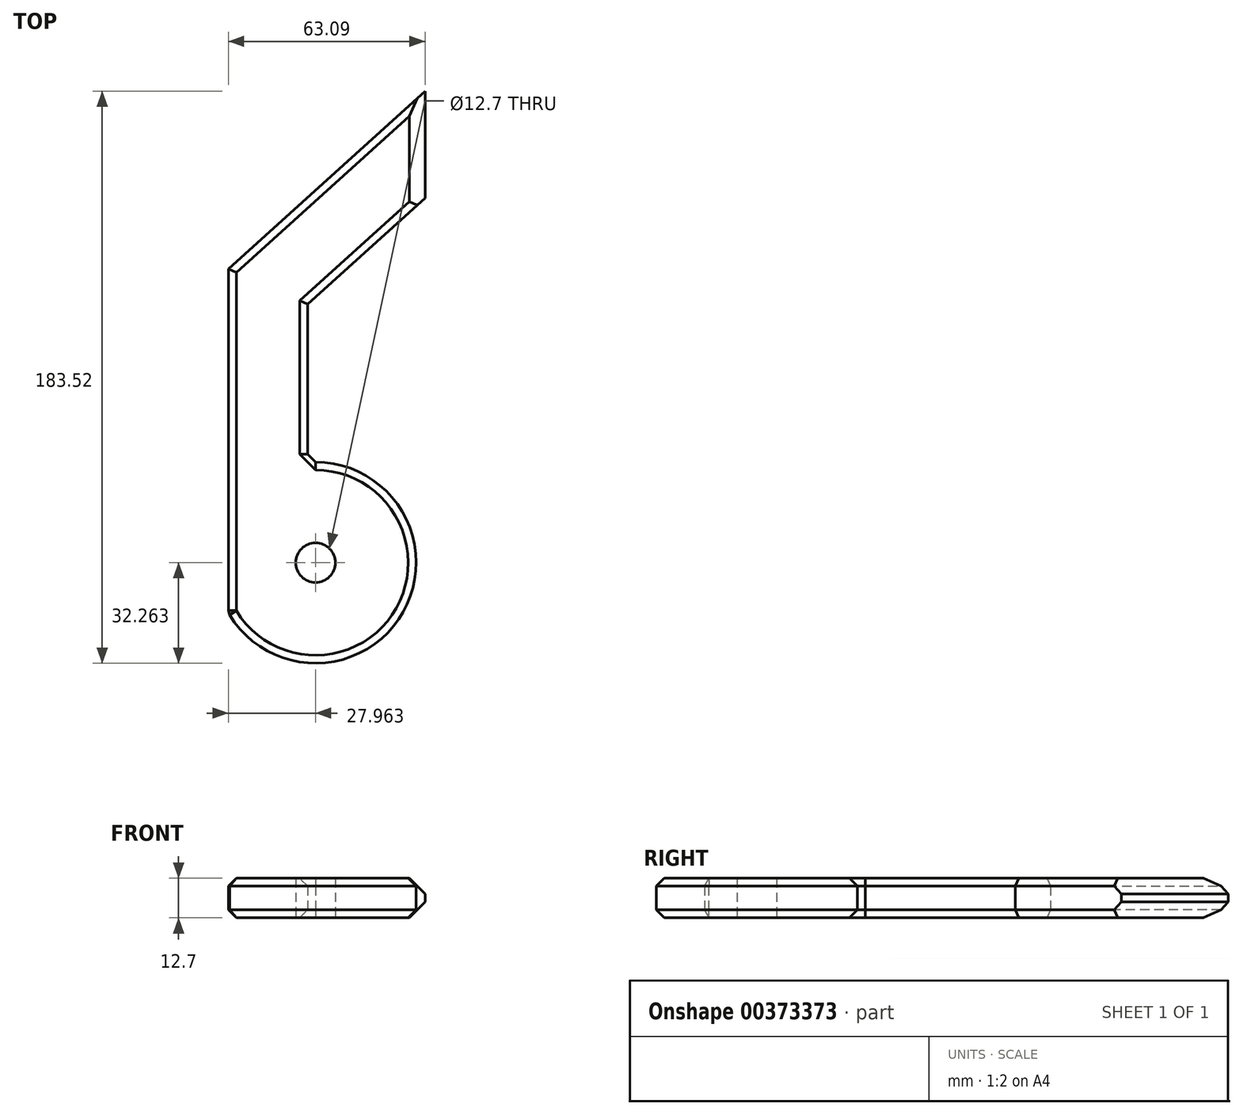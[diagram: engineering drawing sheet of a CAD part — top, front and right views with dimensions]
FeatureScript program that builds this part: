
annotation { "Feature Type Name" : "Feature", "Feature Type Description" : "" }
export const myFeature = defineFeature(function(context is Context, id is Id, definition is map)
    precondition{}
    {
        {
            var Q0;
            Q0=qCreatedBy(makeId("Top.planeOp"),FACE);
            var sketch = newSketch(context, id + "F0", { "sketchPlane" : qUnion([Q0])});
            skLineSegment(sketch, "E0", {"start": v(-39.52, 41.59) * mm, "end": v(-9.18, 69) * mm});
            skLineSegment(sketch, "E1", {"start": v(-9.18, 69) * mm, "end": v(-9.18, 34.77) * mm});
            skLineSegment(sketch, "E2", {"start": v(-9.18, 34.77) * mm, "end": v(-46.87, 0.72) * mm});
            skLineSegment(sketch, "E3", {"start": v(-46.87, 0.72) * mm, "end": v(-46.87, -50.08) * mm});
            skLineSegment(sketch, "E4", {"start": v(-39.52, 41.59) * mm, "end": v(-72.27, 12) * mm});
            skLineSegment(sketch, "E5", {"start": v(-72.27, 12) * mm, "end": v(-72.27, -38.46) * mm});
            skLineSegment(sketch, "E6", {"start": v(-72.27, -38.46) * mm, "end": v(-72.27, -98.35) * mm});
            skArc(sketch, "E7", {"start": v(-72.27, -98.35) * mm, "mid": v(-15.75, -97.27) * mm, "end": v(-46.87, -50.08) * mm});
            skCircle(sketch, "E8", {"center": v(-44.3, -82.25) * mm, "radius": 6.35 * mm});
            skSolve(sketch);
        }
        {
            var Q0;
            Q0=makeQuery(id+"F0.imprint","IMPRINT",FACE,{"disambiguationData":[TD([[makeQuery(id+"F0.imprint","IMPRINT",EDGE,{"derivedFrom":sQuery(id+"F0.wireOp",EDGE,"E0")}),-1.0]])]});
            extrude(context, id + "F1", {"entities" : qUnion([Q0]), "depth" : 12.7 * mm});
        }
        {
            var Q0;
            Q0=makeQuery(id+"F1.opExtrude","CAP_EDGE",EDGE,{"disambiguationData":[OSD([sQuery(id+"F0.wireOp",EDGE,"E1")])],"isStart":false});
            var Q1;
            Q1=makeQuery(id+"F1.opExtrude","CAP_EDGE",EDGE,{"disambiguationData":[OSD([sQuery(id+"F0.wireOp",EDGE,"E1")])],"isStart":true});
            chamfer(context, id + "F2", {"entities" : qUnion([Q0, Q1]), "chamferType" : ChamferType.OFFSET_ANGLE, "width" : 5.08 * mm, "oppositeDirection" : false, "angle" : 45 * degree, "tangentPropagation" : true});
        }
        {
            var Q0;
            Q0=makeQuery(id+"F1.opExtrude","CAP_EDGE",EDGE,{"disambiguationData":[OSD([sQuery(id+"F0.wireOp",EDGE,"E3")])],"isStart":false});
            var Q1;
            Q1=makeQuery(id+"F1.opExtrude","CAP_EDGE",EDGE,{"disambiguationData":[OSD([sQuery(id+"F0.wireOp",EDGE,"E3")])],"isStart":true});
            var Q2;
            Q2=makeQuery(id+"F1.opExtrude","CAP_EDGE",EDGE,{"disambiguationData":[OSD([sQuery(id+"F0.wireOp",EDGE,"E2")])],"isStart":false});
            var Q3;
            Q3=makeQuery(id+"F1.opExtrude","CAP_EDGE",EDGE,{"disambiguationData":[OSD([sQuery(id+"F0.wireOp",EDGE,"E2")])],"isStart":true});
            var Q4;
            Q4=makeQuery(id+"F1.opExtrude","CAP_EDGE",EDGE,{"disambiguationData":[OSD([sQuery(id+"F0.wireOp",EDGE,"E7")])],"isStart":false});
            var Q5;
            Q5=makeQuery(id+"F1.opExtrude","SWEPT_FACE",FACE,{"disambiguationData":[OSD([sQuery(id+"F0.wireOp",EDGE,"E7")])]});
            var Q6;
            Q6=makeQuery(id+"F1.opExtrude","CAP_EDGE",EDGE,{"disambiguationData":[OSD([sQuery(id+"F0.wireOp",EDGE,"E5"),sQuery(id+"F0.wireOp",EDGE,"E6")])],"isStart":false});
            var Q7;
            Q7=makeQuery(id+"F1.opExtrude","CAP_EDGE",EDGE,{"disambiguationData":[OSD([sQuery(id+"F0.wireOp",EDGE,"E5"),sQuery(id+"F0.wireOp",EDGE,"E6")])],"isStart":true});
            var Q8;
            Q8=makeQuery(id+"F1.opExtrude","CAP_EDGE",EDGE,{"disambiguationData":[OSD([sQuery(id+"F0.wireOp",EDGE,"E0"),sQuery(id+"F0.wireOp",EDGE,"E4")])],"isStart":false});
            var Q9;
            Q9=makeQuery(id+"F1.opExtrude","CAP_EDGE",EDGE,{"disambiguationData":[OSD([sQuery(id+"F0.wireOp",EDGE,"E0"),sQuery(id+"F0.wireOp",EDGE,"E4")])],"isStart":true});
            chamfer(context, id + "F3", {"entities" : qUnion([Q0, Q1, Q2, Q3, Q4, Q5, Q6, Q7, Q8, Q9]), "width" : 2.54 * mm, "tangentPropagation" : true});
        }
    });
